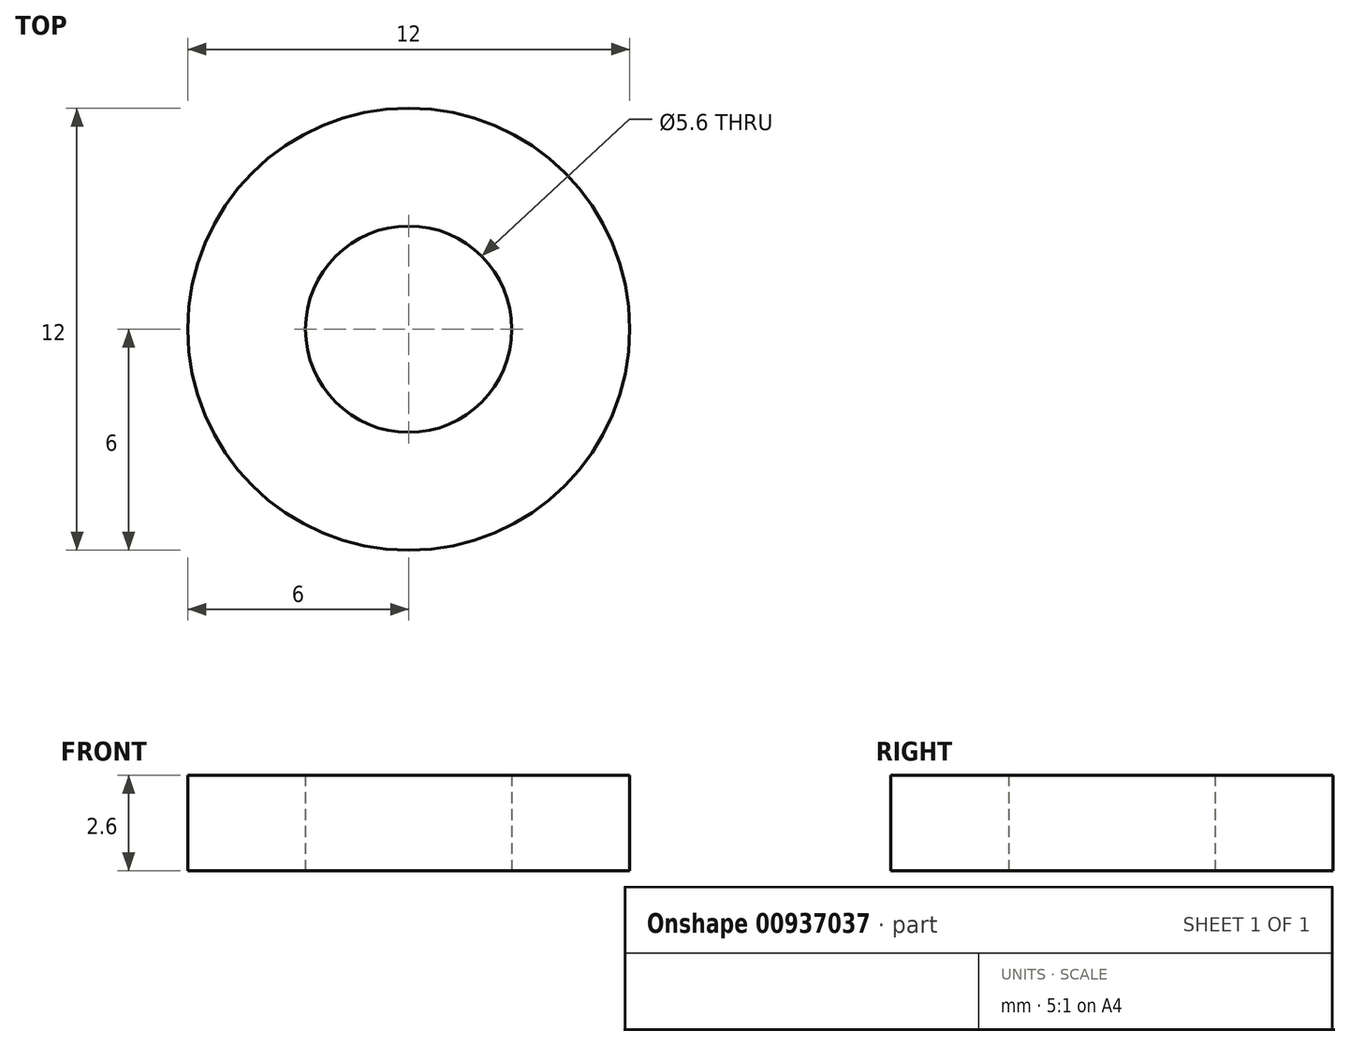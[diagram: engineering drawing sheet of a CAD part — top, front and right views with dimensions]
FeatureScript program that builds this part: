
annotation { "Feature Type Name" : "Feature", "Feature Type Description" : "" }
export const myFeature = defineFeature(function(context is Context, id is Id, definition is map)
    precondition{}
    {
        {
            var Q0;
            Q0=qCreatedBy(makeId("Top.planeOp"),FACE);
            var sketch = newSketch(context, id + "F0", { "sketchPlane" : qUnion([Q0])});
            skCircle(sketch, "E0", {"center": v(0, 0) * mm, "radius": 6 * mm});
            skCircle(sketch, "E1", {"center": v(0, 0) * mm, "radius": 2.8 * mm});
            skSolve(sketch);
        }
        {
            var Q0;
            Q0 = qSketchRegion(id + "F0", true);
            extrude(context, id + "F1", {"entities" : qUnion([Q0]), "depth" : 2.6 * mm, "offsetDistance" : 25 * mm});
        }
    });
